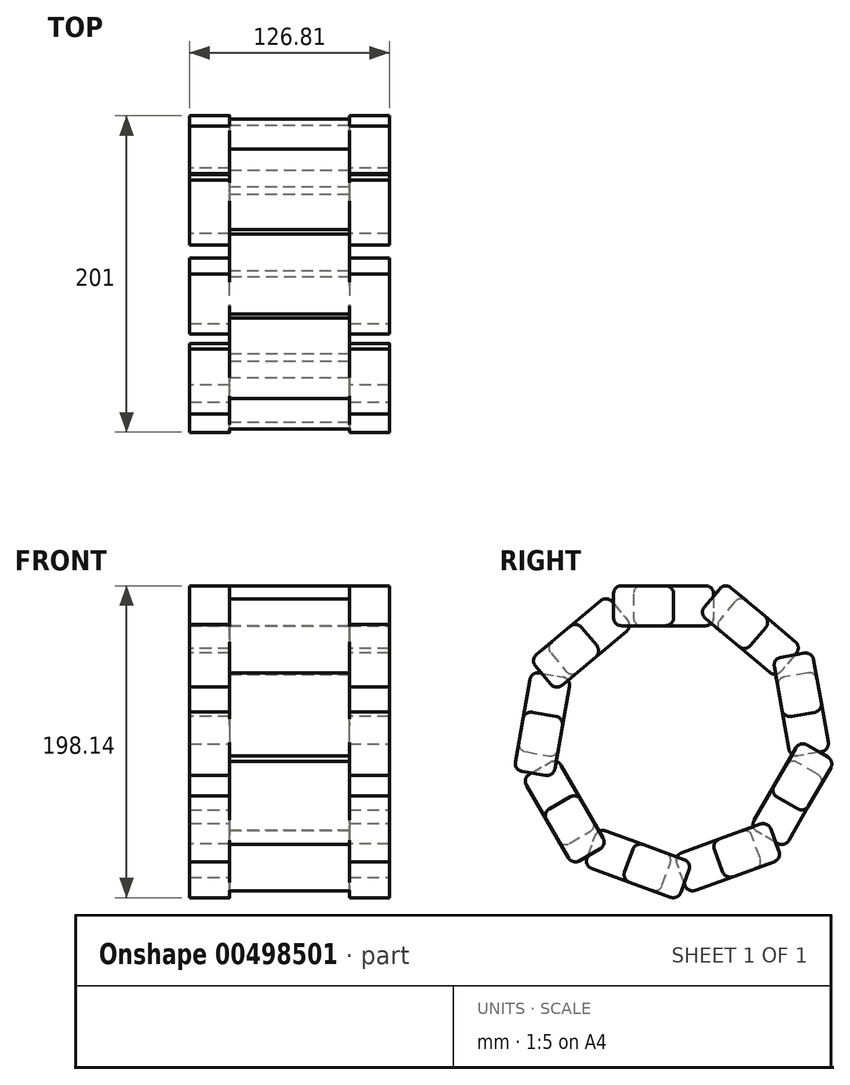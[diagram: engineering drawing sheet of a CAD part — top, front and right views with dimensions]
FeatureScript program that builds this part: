
annotation { "Feature Type Name" : "Feature", "Feature Type Description" : "" }
export const myFeature = defineFeature(function(context is Context, id is Id, definition is map)
    precondition{}
    {
        {
            var Q0;
            Q0=qCreatedBy(makeId("Top.planeOp"),FACE);
            var sketch = newSketch(context, id + "F0", { "sketchPlane" : qUnion([Q0])});
            skLineSegment(sketch, "E0", {"start": v(-24.46, 25.4) * mm, "end": v(51.74, 25.4) * mm});
            skLineSegment(sketch, "E1", {"start": v(51.74, 25.4) * mm, "end": v(51.74, 0) * mm});
            skLineSegment(sketch, "E2", {"start": v(51.74, 0) * mm, "end": v(77.14, 0) * mm});
            skLineSegment(sketch, "E3", {"start": v(77.14, 0) * mm, "end": v(77.14, -38.1) * mm});
            skLineSegment(sketch, "E4", {"start": v(77.14, -38.1) * mm, "end": v(51.74, -38.1) * mm});
            skLineSegment(sketch, "E5", {"start": v(51.74, -38.1) * mm, "end": v(51.74, -25.4) * mm});
            skLineSegment(sketch, "E6", {"start": v(51.74, -25.4) * mm, "end": v(-24.27, -25.4) * mm});
            skLineSegment(sketch, "E7", {"start": v(-24.27, -25.4) * mm, "end": v(-24.27, -38.1) * mm});
            skLineSegment(sketch, "E8", {"start": v(-24.27, -38.1) * mm, "end": v(-49.67, -38.1) * mm});
            skLineSegment(sketch, "E9", {"start": v(-49.67, -38.1) * mm, "end": v(-49.67, 0) * mm});
            skLineSegment(sketch, "E10", {"start": v(-49.67, 0) * mm, "end": v(-24.27, 0) * mm});
            skLineSegment(sketch, "E11", {"start": v(-24.27, 0) * mm, "end": v(-24.46, 25.4) * mm});
            skSolve(sketch);
        }
        {
            var Q0;
            Q0=makeQuery(id+"F0.imprint","IMPRINT",FACE,{"disambiguationData":[TD([[makeQuery(id+"F0.imprint","IMPRINT",EDGE,{"derivedFrom":sQuery(id+"F0.wireOp",EDGE,"E0")}),-1.0]])]});
            extrude(context, id + "F1", {"entities" : qUnion([Q0]), "depth" : 25.4 * mm});
        }
        {
            var Q0;
            Q0=makeQuery(id+"F1.opExtrude","CAP_EDGE",EDGE,{"disambiguationData":[OSD([sQuery(id+"F0.wireOp",EDGE,"E0")])],"isStart":false});
            var Q1;
            Q1=makeQuery(id+"F1.opExtrude","CAP_EDGE",EDGE,{"disambiguationData":[OSD([sQuery(id+"F0.wireOp",EDGE,"E0")])],"isStart":true});
            var Q2;
            Q2=makeQuery(id+"F1.opExtrude","CAP_EDGE",EDGE,{"disambiguationData":[OSD([sQuery(id+"F0.wireOp",EDGE,"E6")])],"isStart":true});
            var Q3;
            Q3=makeQuery(id+"F1.opExtrude","CAP_EDGE",EDGE,{"disambiguationData":[OSD([sQuery(id+"F0.wireOp",EDGE,"E6")])],"isStart":false});
            var Q4;
            Q4=makeQuery(id+"F1.opExtrude","CAP_EDGE",EDGE,{"disambiguationData":[OSD([sQuery(id+"F0.wireOp",EDGE,"E4")])],"isStart":false});
            var Q5;
            Q5=makeQuery(id+"F1.opExtrude","CAP_EDGE",EDGE,{"disambiguationData":[OSD([sQuery(id+"F0.wireOp",EDGE,"E8")])],"isStart":false});
            var Q6;
            Q6=makeQuery(id+"F1.opExtrude","CAP_EDGE",EDGE,{"disambiguationData":[OSD([sQuery(id+"F0.wireOp",EDGE,"E8")])],"isStart":true});
            var Q7;
            Q7=makeQuery(id+"F1.opExtrude","CAP_EDGE",EDGE,{"disambiguationData":[OSD([sQuery(id+"F0.wireOp",EDGE,"E4")])],"isStart":true});
            var Q8;
            Q8=makeQuery(id+"F1.opExtrude","CAP_EDGE",EDGE,{"disambiguationData":[OSD([sQuery(id+"F0.wireOp",EDGE,"E2")])],"isStart":true});
            var Q9;
            Q9=makeQuery(id+"F1.opExtrude","CAP_EDGE",EDGE,{"disambiguationData":[OSD([sQuery(id+"F0.wireOp",EDGE,"E2")])],"isStart":false});
            var Q10;
            Q10=makeQuery(id+"F1.opExtrude","CAP_EDGE",EDGE,{"disambiguationData":[OSD([sQuery(id+"F0.wireOp",EDGE,"E10")])],"isStart":false});
            var Q11;
            Q11=makeQuery(id+"F1.opExtrude","CAP_EDGE",EDGE,{"disambiguationData":[OSD([sQuery(id+"F0.wireOp",EDGE,"E10")])],"isStart":true});
            fillet(context, id + "F2", {"entities" : qUnion([Q0, Q1, Q2, Q3, Q4, Q5, Q6, Q7, Q8, Q9, Q10, Q11]), "radius" : 5.08 * mm, "tangentPropagation" : true, "allowEdgeOverflow" : false});
        }
        {
            var Q0;
            Q0=qCreatedBy(makeId("Right.planeOp"),FACE);
            var sketch = newSketch(context, id + "F3", { "sketchPlane" : qUnion([Q0])});
            skCircle(sketch, "E12", {"center": v(0, -70.77) * mm, "radius": 84.43 * mm});
            skSolve(sketch);
        }
        {
            var Q0;
            Q0=makeQuery(id+"F1.opExtrude","SWEPT_BODY",BODY,{"disambiguationData":[OSD([sQuery(id+"F0.wireOp",EDGE,"E0"),sQuery(id+"F0.wireOp",EDGE,"E1"),sQuery(id+"F0.wireOp",EDGE,"E2"),sQuery(id+"F0.wireOp",EDGE,"E3"),sQuery(id+"F0.wireOp",EDGE,"E4"),sQuery(id+"F0.wireOp",EDGE,"E5"),sQuery(id+"F0.wireOp",EDGE,"E6"),sQuery(id+"F0.wireOp",EDGE,"E7"),sQuery(id+"F0.wireOp",EDGE,"E8"),sQuery(id+"F0.wireOp",EDGE,"E9"),sQuery(id+"F0.wireOp",EDGE,"E10"),sQuery(id+"F0.wireOp",EDGE,"E11")])]});
            var Q1;
            Q1=sQuery(id+"F3.wireOp",EDGE,"E12");
            circularPattern(context, id + "F4", {"entities" : qUnion([Q0]), "axis" : qUnion([Q1]), "angle" : 360 * degree, "instanceCount" : 9, "equalSpace" : true});
        }
    });
